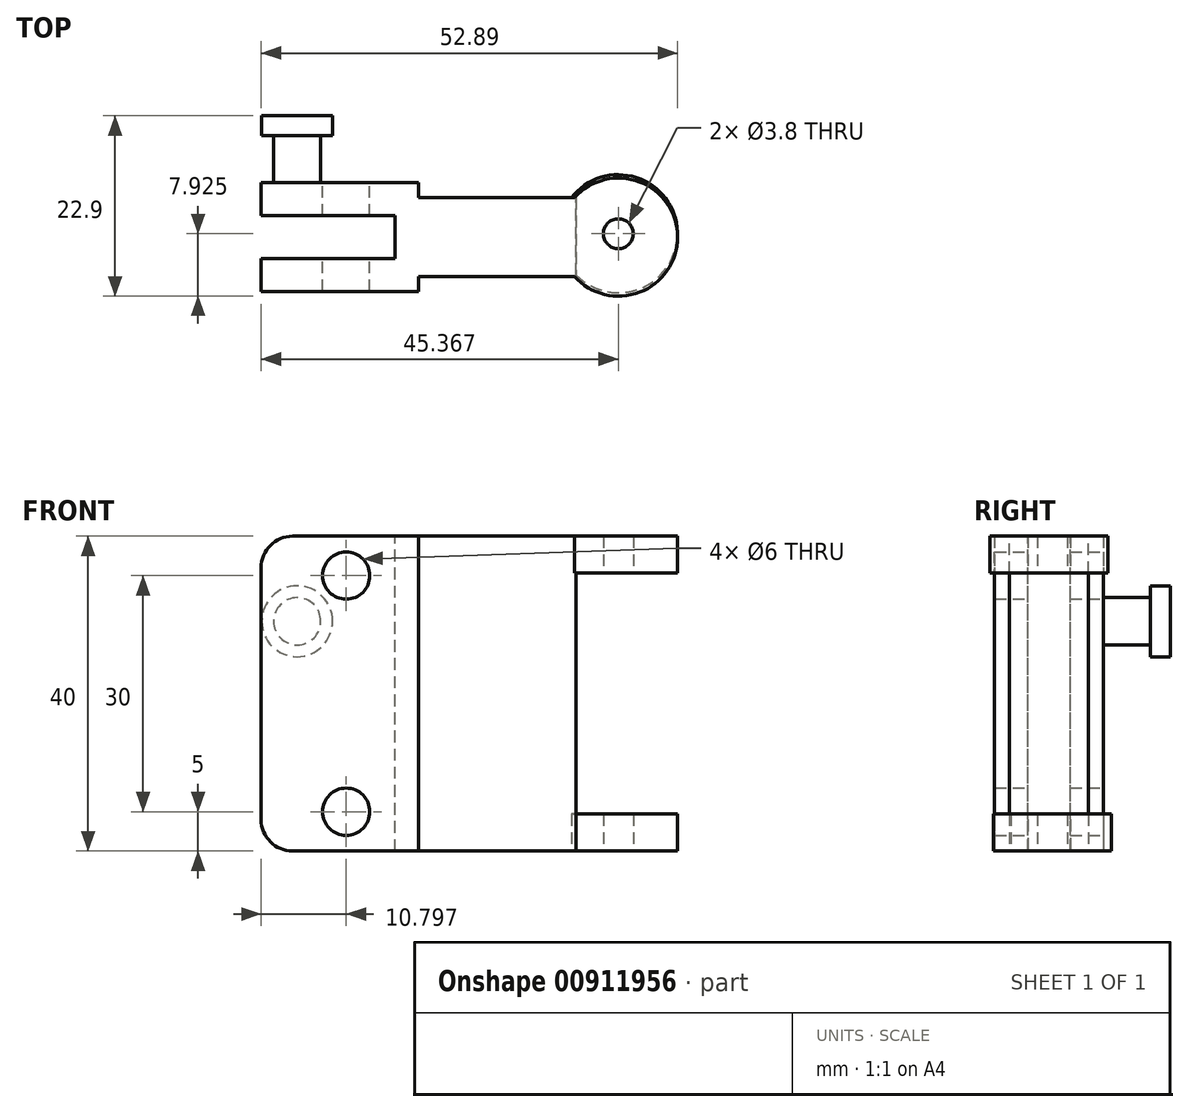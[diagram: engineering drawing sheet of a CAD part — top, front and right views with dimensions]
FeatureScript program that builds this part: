
annotation { "Feature Type Name" : "Feature", "Feature Type Description" : "" }
export const myFeature = defineFeature(function(context is Context, id is Id, definition is map)
    precondition{}
    {
        {
            var Q0;
            Q0=qCreatedBy(makeId("Front.planeOp"),FACE);
            var sketch = newSketch(context, id + "F0", { "sketchPlane" : qUnion([Q0])});
            skLineSegment(sketch, "E0.bottom", {"start": v(-3.61, 30.62) * mm, "end": v(11.39, 30.62) * mm});
            skLineSegment(sketch, "E0.top", {"start": v(-3.61, -9.38) * mm, "end": v(11.39, -9.38) * mm});
            skLineSegment(sketch, "E0.left", {"start": v(-3.61, 30.62) * mm, "end": v(-3.61, -9.38) * mm});
            skLineSegment(sketch, "E0.right", {"start": v(16.39, 25.62) * mm, "end": v(16.39, 5.62) * mm});
            skPoint(sketch, "E1.visualSharp", {"position": v(16.39, 30.62) * mm});
            skPoint(sketch, "E2.visualSharp", {"position": v(16.39, -9.38) * mm});
            skLineSegment(sketch, "E3", {"start": v(11.39, 30.62) * mm, "end": v(16.39, 30.62) * mm});
            skLineSegment(sketch, "E4", {"start": v(16.39, 25.62) * mm, "end": v(16.39, 30.62) * mm});
            skLineSegment(sketch, "E5", {"start": v(11.39, -9.38) * mm, "end": v(16.39, -9.38) * mm});
            skLineSegment(sketch, "E6", {"start": v(16.39, 5.62) * mm, "end": v(16.39, -9.38) * mm});
            skSolve(sketch);
        }
        {
            var Q0;
            Q0 = qSketchRegion(id + "F0", true);
            extrude(context, id + "F1", {"entities" : qUnion([Q0]), "depth" : 13.8 * mm, "offsetDistance" : 25 * mm});
        }
        {
            var Q0;
            Q0=makeQuery(id+"F1.opExtrude","SWEPT_FACE",FACE,{"disambiguationData":[OSD([sQuery(id+"F0.wireOp",EDGE,"E0.left")])]});
            var sketch = newSketch(context, id + "F2", { "sketchPlane" : qUnion([Q0])});
            skLineSegment(sketch, "E7.bottom", {"start": v(4.2, -9.38) * mm, "end": v(9.6, -9.38) * mm});
            skLineSegment(sketch, "E7.top", {"start": v(4.2, 30.62) * mm, "end": v(9.6, 30.62) * mm});
            skLineSegment(sketch, "E7.left", {"start": v(4.2, -9.38) * mm, "end": v(4.2, 30.62) * mm});
            skLineSegment(sketch, "E7.right", {"start": v(9.6, -9.38) * mm, "end": v(9.6, 30.62) * mm});
            skSolve(sketch);
        }
        {
            var Q0;
            Q0=makeQuery(id+"F2.imprint","IMPRINT",FACE,{"disambiguationData":[TD([[makeQuery(id+"F2.imprint","IMPRINT",EDGE,{"derivedFrom":sQuery(id+"F2.wireOp",EDGE,"E7.bottom")}),-1.0]])]});
            extrude(context, id + "F3", {"entities" : qUnion([Q0]), "operationType" : NewBodyOperationType.REMOVE, "oppositeDirection" : true, "depth" : 17 * mm, "offsetDistance" : 25 * mm});
        }
        {
            var Q0;
            Q0=makeQuery(id+"F1.opExtrude","CAP_FACE",FACE,{"disambiguationData":[OSD([sQuery(id+"F0.wireOp",EDGE,"E0.bottom"),sQuery(id+"F0.wireOp",EDGE,"E0.top"),sQuery(id+"F0.wireOp",EDGE,"E0.left"),sQuery(id+"F0.wireOp",EDGE,"E0.right"),sQuery(id+"F0.wireOp",EDGE,"E4"),sQuery(id+"F0.wireOp",EDGE,"E6")])],"isStart":true});
            var sketch = newSketch(context, id + "F4", { "sketchPlane" : qUnion([Q0])});
            skCircle(sketch, "E8", {"center": v(-7.19, 25.62) * mm, "radius": 3 * mm});
            skCircle(sketch, "E9", {"center": v(-7.19, -4.38) * mm, "radius": 3 * mm});
            skSolve(sketch);
        }
        {
            var Q0;
            Q0 = qSketchRegion(id + "F4", true);
            extrude(context, id + "F5", {"entities" : qUnion([Q0]), "operationType" : NewBodyOperationType.REMOVE, "oppositeDirection" : true, "depth" : 25 * mm, "offsetDistance" : 25 * mm});
        }
        {
            var Q0;
            Q0=makeQuery(id+"F0.imprint","IMPRINT",FACE,{"disambiguationData":[TD([[makeQuery(id+"F0.imprint","IMPRINT",EDGE,{"derivedFrom":sQuery(id+"F0.wireOp",EDGE,"E0.bottom")}),-1.0]])]});
            var sketch = newSketch(context, id + "F6", { "sketchPlane" : qUnion([Q0])});
            skCircle(sketch, "E10", {"center": v(0.96, 19.8) * mm, "radius": 3 * mm});
            skSolve(sketch);
        }
        {
            var Q0;
            Q0 = qSketchRegion(id + "F6", true);
            extrude(context, id + "F7", {"entities" : qUnion([Q0]), "oppositeDirection" : true, "depth" : 6 * mm, "offsetDistance" : 25 * mm});
        }
        {
            var Q0;
            Q0=makeQuery(id+"F7.opExtrude","CAP_FACE",FACE,{"disambiguationData":[OSD([sQuery(id+"F6.wireOp",EDGE,"E10")])],"isStart":false});
            var sketch = newSketch(context, id + "F8", { "sketchPlane" : qUnion([Q0])});
            skCircle(sketch, "E11", {"center": v(-0.96, 19.8) * mm, "radius": 4.5 * mm});
            skSolve(sketch);
        }
        {
            var Q0;
            Q0 = qSketchRegion(id + "F8", true);
            extrude(context, id + "F9", {"entities" : qUnion([Q0]), "operationType" : NewBodyOperationType.ADD, "depth" : 2.5 * mm, "offsetDistance" : 25 * mm});
        }
        {
            var Q0;
            {var subQ1=sQuery(id+"F0.wireOp",EDGE,"E0.left");var subQ2=sQuery(id+"F0.wireOp",EDGE,"E0.bottom");Q0=makeQuery(id+"F3.boolean.opBoolean","SPLIT",EDGE,{"disambiguationData":[TD([makeQuery(id+"F3.opExtrude","SWEPT_FACE",FACE,{"disambiguationData":[OSD([sQuery(id+"F2.wireOp",EDGE,"E7.left")])]})])],"derivedFrom":makeQuery(id+"F1.opExtrude","SWEPT_EDGE",EDGE,{"disambiguationData":[OSD([subQ2,subQ1])]})});}
            var Q1;
            {var subQ1=sQuery(id+"F0.wireOp",EDGE,"E0.left");var subQ2=sQuery(id+"F0.wireOp",EDGE,"E0.bottom");Q1=makeQuery(id+"F3.boolean.opBoolean","SPLIT",EDGE,{"disambiguationData":[TD([makeQuery(id+"F3.opExtrude","SWEPT_FACE",FACE,{"disambiguationData":[OSD([sQuery(id+"F2.wireOp",EDGE,"E7.right")])]})])],"derivedFrom":makeQuery(id+"F1.opExtrude","SWEPT_EDGE",EDGE,{"disambiguationData":[OSD([subQ2,subQ1])]})});}
            var Q2;
            {var subQ1=sQuery(id+"F0.wireOp",EDGE,"E0.left");var subQ2=sQuery(id+"F0.wireOp",EDGE,"E0.top");Q2=makeQuery(id+"F3.boolean.opBoolean","SPLIT",EDGE,{"disambiguationData":[TD([makeQuery(id+"F3.opExtrude","SWEPT_FACE",FACE,{"disambiguationData":[OSD([sQuery(id+"F2.wireOp",EDGE,"E7.left")])]})])],"derivedFrom":makeQuery(id+"F1.opExtrude","SWEPT_EDGE",EDGE,{"disambiguationData":[OSD([subQ2,subQ1])]})});}
            var Q3;
            {var subQ1=sQuery(id+"F0.wireOp",EDGE,"E0.left");var subQ2=sQuery(id+"F0.wireOp",EDGE,"E0.top");Q3=makeQuery(id+"F3.boolean.opBoolean","SPLIT",EDGE,{"disambiguationData":[TD([makeQuery(id+"F3.opExtrude","SWEPT_FACE",FACE,{"disambiguationData":[OSD([sQuery(id+"F2.wireOp",EDGE,"E7.right")])]})])],"derivedFrom":makeQuery(id+"F1.opExtrude","SWEPT_EDGE",EDGE,{"disambiguationData":[OSD([subQ2,subQ1])]})});}
            fillet(context, id + "F10", {"entities" : qUnion([Q0, Q1, Q2, Q3]), "radius" : 4 * mm, "tangentPropagation" : true, "allowEdgeOverflow" : false});
        }
        {
            var Q0;
            Q0=makeQuery(id+"F1.opExtrude","SWEPT_FACE",FACE,{"disambiguationData":[OSD([sQuery(id+"F0.wireOp",EDGE,"E0.right"),sQuery(id+"F0.wireOp",EDGE,"E4"),sQuery(id+"F0.wireOp",EDGE,"E6")])]});
            var sketch = newSketch(context, id + "F11", { "sketchPlane" : qUnion([Q0])});
            skLineSegment(sketch, "E12.bottom", {"start": v(-11.9, 30.62) * mm, "end": v(-1.9, 30.62) * mm});
            skLineSegment(sketch, "E12.top", {"start": v(-11.9, -9.38) * mm, "end": v(-1.9, -9.38) * mm});
            skLineSegment(sketch, "E12.left", {"start": v(-11.9, 30.62) * mm, "end": v(-11.9, -9.38) * mm});
            skLineSegment(sketch, "E12.right", {"start": v(-1.9, 30.62) * mm, "end": v(-1.9, -9.38) * mm});
            skSolve(sketch);
        }
        {
            var Q0;
            Q0 = qSketchRegion(id + "F11", true);
            extrude(context, id + "F12", {"entities" : qUnion([Q0]), "operationType" : NewBodyOperationType.ADD, "depth" : 20 * mm, "offsetDistance" : 25 * mm});
        }
        {
            var Q0;
            Q0=makeQuery(id+"F12.boolean.opBoolean","MERGE",FACE,{"derivedFrom":[makeQuery(id+"F1.opExtrude","SWEPT_FACE",FACE,{"disambiguationData":[OSD([sQuery(id+"F0.wireOp",EDGE,"E0.bottom"),sQuery(id+"F0.wireOp",EDGE,"E3")])]}),makeQuery(id+"F12.opExtrude","SWEPT_FACE",FACE,{"disambiguationData":[OSD([sQuery(id+"F11.wireOp",EDGE,"E12.bottom")])]})]});
            var sketch = newSketch(context, id + "F13", { "sketchPlane" : qUnion([Q0])});
            skCircle(sketch, "E13", {"center": v(41.78, -6.9) * mm, "radius": 7.5 * mm});
            skPoint(sketch, "E14", {"position": v(36.39, -6.9) * mm});
            skSolve(sketch);
        }
        {
            var Q0;
            Q0 = qSketchRegion(id + "F13", true);
            extrude(context, id + "F14", {"entities" : qUnion([Q0]), "operationType" : NewBodyOperationType.ADD, "oppositeDirection" : true, "depth" : 4.7 * mm, "offsetDistance" : 25 * mm});
        }
        {
            var Q0;
            Q0=makeQuery(id+"F12.boolean.opBoolean","MERGE",FACE,{"derivedFrom":[makeQuery(id+"F1.opExtrude","SWEPT_FACE",FACE,{"disambiguationData":[OSD([sQuery(id+"F0.wireOp",EDGE,"E0.top"),sQuery(id+"F0.wireOp",EDGE,"E5")])]}),makeQuery(id+"F12.opExtrude","SWEPT_FACE",FACE,{"disambiguationData":[OSD([sQuery(id+"F11.wireOp",EDGE,"E12.top")])]})]});
            var sketch = newSketch(context, id + "F15", { "sketchPlane" : qUnion([Q0])});
            skCircle(sketch, "E15", {"center": v(41.76, 6.48) * mm, "radius": 7.5 * mm});
            skSolve(sketch);
        }
        {
            var Q0;
            Q0 = qSketchRegion(id + "F15", true);
            extrude(context, id + "F16", {"entities" : qUnion([Q0]), "operationType" : NewBodyOperationType.ADD, "oppositeDirection" : true, "depth" : 4.7 * mm, "offsetDistance" : 25 * mm});
        }
        {
            var Q0;
            Q0=makeQuery(id+"F16.boolean.opBoolean","MERGE",FACE,{"derivedFrom":[makeQuery(id+"F12.boolean.opBoolean","MERGE",FACE,{"derivedFrom":[makeQuery(id+"F1.opExtrude","SWEPT_FACE",FACE,{"disambiguationData":[OSD([sQuery(id+"F0.wireOp",EDGE,"E0.top"),sQuery(id+"F0.wireOp",EDGE,"E5")])]}),makeQuery(id+"F12.opExtrude","SWEPT_FACE",FACE,{"disambiguationData":[OSD([sQuery(id+"F11.wireOp",EDGE,"E12.top")])]})]}),makeQuery(id+"F16.opExtrude","CAP_FACE",FACE,{"disambiguationData":[OSD([sQuery(id+"F15.wireOp",EDGE,"E15")])],"isStart":true})]});
            var sketch = newSketch(context, id + "F17", { "sketchPlane" : qUnion([Q0])});
            skCircle(sketch, "E16", {"center": v(41.76, 6.48) * mm, "radius": 1.9 * mm});
            skSolve(sketch);
        }
        {
            var Q0;
            Q0 = qSketchRegion(id + "F17", true);
            extrude(context, id + "F18", {"entities" : qUnion([Q0]), "operationType" : NewBodyOperationType.REMOVE, "oppositeDirection" : true, "depth" : 70 * mm, "offsetDistance" : 25 * mm});
        }
    });
